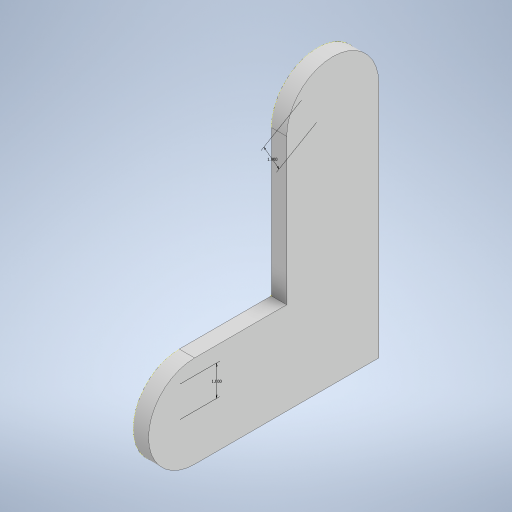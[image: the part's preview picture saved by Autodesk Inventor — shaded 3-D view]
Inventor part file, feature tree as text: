
AUTODESK INVENTOR PART (.ipt)
format: ipt  version: 2023 (Build 270158000, 158)  size: 249,856 bytes
history: native  units: in
note: dims shown in document units (in); Inventor stores cm internally (conversion verified against a paired STEP export)
features: sketch x2, extrude x1, plane x1
ambient origin geometry x8: Origin, YZ Plane, XZ Plane, XY Plane, X Axis, Y Axis, Z Axis, Center Point
bodies: Solid1 (feature_tree)
feature tree (4):
  extrude  "Extrusion1"  Depth=3.0in
  plane  "Work Plane1"
  sketch  "Sketch2"  dims[d5=0.5in d6=0.0in d7=0.0in d8=4.75in d9=0.0in d10=3.0in d11=1.0in d12=1.0in d13=1.0in]
  sketch  "Sketch1"  dims[d1=3.0in d2=3.0in]
